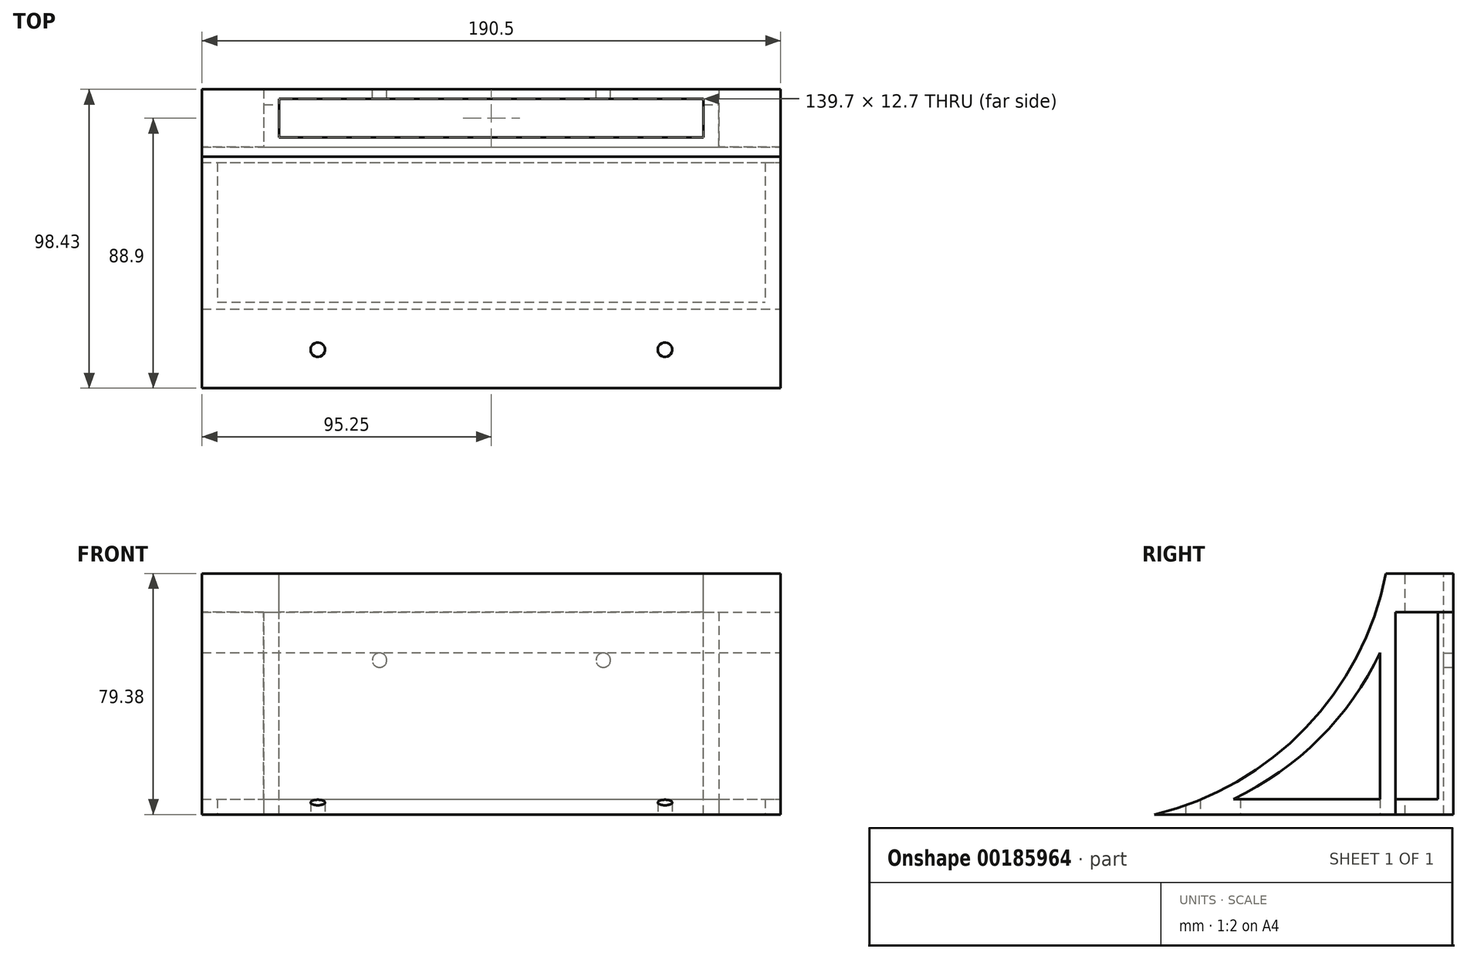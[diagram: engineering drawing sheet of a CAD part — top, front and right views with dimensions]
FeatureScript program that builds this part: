
annotation { "Feature Type Name" : "Feature", "Feature Type Description" : "" }
export const myFeature = defineFeature(function(context is Context, id is Id, definition is map)
    precondition{}
    {
        {
            var Q0;
            Q0=qCreatedBy(makeId("Right.planeOp"),FACE);
            var sketch = newSketch(context, id + "F0", { "sketchPlane" : qUnion([Q0])});
            skLineSegment(sketch, "E0", {"start": v(0, 0) * mm, "end": v(-76.2, 0) * mm});
            skLineSegment(sketch, "E1", {"start": v(0, 0) * mm, "end": v(0, 79.38) * mm});
            skArc(sketch, "E2", {"start": v(-76.2, 0) * mm, "mid": v(-26.42, 28.48) * mm, "end": v(0, 79.38) * mm});
            skSolve(sketch);
        }
        {
            var Q0;
            Q0 = qSketchRegion(id + "F0", true);
            extrude(context, id + "F1", {"entities" : qUnion([Q0]), "depth" : 190.5 * mm});
        }
        {
            var Q0;
            Q0=makeQuery(id+"F1.opExtrude","SWEPT_FACE",FACE,{"disambiguationData":[OSD([sQuery(id+"F0.wireOp",EDGE,"E1")])]});
            var sketch = newSketch(context, id + "F2", { "sketchPlane" : qUnion([Q0])});
            skSolve(sketch);
        }
        {
            var Q0;
            Q0 = qSketchRegion(id + "F2", true);
            var Q1;
            {var subQ0=sQuery(id+"F0.wireOp",EDGE,"E1");Q1=makeQuery(id+"F2.imprint","IMPRINT",FACE,{"disambiguationData":[TD([[makeQuery(id+"F2.imprint","IMPRINT",EDGE,{"derivedFrom":makeQuery(id+"F1.opExtrude","CAP_EDGE",EDGE,{"disambiguationData":[OSD([subQ0])],"isStart":true})}),1.0]])]});}
            extrude(context, id + "F3", {"entities" : qUnion([Q0, Q1]), "operationType" : NewBodyOperationType.ADD, "depth" : 3.17 * mm});
        }
        {
            var Q0;
            Q0=makeQuery(id+"F3.opExtrude","CAP_FACE",FACE,{"disambiguationData":[OSD([sQuery(id+"F0.wireOp",EDGE,"E0"),sQuery(id+"F0.wireOp",EDGE,"E1"),sQuery(id+"F0.wireOp",EDGE,"E2")])],"isStart":false});
            var sketch = newSketch(context, id + "F4", { "sketchPlane" : qUnion([Q0])});
            skLineSegment(sketch, "E3.bottom", {"start": v(-170.18, 79.38) * mm, "end": v(-20.32, 79.38) * mm});
            skLineSegment(sketch, "E3.top", {"start": v(-170.18, 0) * mm, "end": v(-20.32, 0) * mm});
            skLineSegment(sketch, "E3.left", {"start": v(-170.18, 79.38) * mm, "end": v(-170.18, 0) * mm});
            skLineSegment(sketch, "E3.right", {"start": v(-20.32, 79.38) * mm, "end": v(-20.32, 0) * mm});
            skSolve(sketch);
        }
        {
            var Q0;
            Q0=makeQuery(id+"F4.imprint","IMPRINT",FACE,{"disambiguationData":[TD([[makeQuery(id+"F4.imprint","IMPRINT",EDGE,{"derivedFrom":sQuery(id+"F4.wireOp",EDGE,"E3.bottom")}),-1.0]])]});
            extrude(context, id + "F5", {"entities" : qUnion([Q0]), "operationType" : NewBodyOperationType.ADD, "depth" : 19.05 * mm});
        }
        {
            var Q0;
            Q0=makeQuery(id+"F5.boolean.opBoolean","MERGE",FACE,{"derivedFrom":[makeQuery(id+"F3.opExtrude","SWEPT_FACE",FACE,{"disambiguationData":[OSD([sQuery(id+"F0.wireOp",EDGE,"E1"),sQuery(id+"F0.wireOp",EDGE,"E2")])]}),makeQuery(id+"F5.opExtrude","SWEPT_FACE",FACE,{"disambiguationData":[OSD([sQuery(id+"F4.wireOp",EDGE,"E3.bottom")])]})]});
            var sketch = newSketch(context, id + "F6", { "sketchPlane" : qUnion([Q0])});
            skLineSegment(sketch, "E4.bottom", {"start": v(25.4, 19.05) * mm, "end": v(165.1, 19.05) * mm});
            skLineSegment(sketch, "E4.top", {"start": v(25.4, 6.35) * mm, "end": v(165.1, 6.35) * mm});
            skLineSegment(sketch, "E4.left", {"start": v(25.4, 19.05) * mm, "end": v(25.4, 6.35) * mm});
            skLineSegment(sketch, "E4.right", {"start": v(165.1, 19.05) * mm, "end": v(165.1, 6.35) * mm});
            skSolve(sketch);
        }
        {
            var Q0;
            Q0 = qSketchRegion(id + "F6", true);
            extrude(context, id + "F7", {"entities" : qUnion([Q0]), "operationType" : NewBodyOperationType.REMOVE, "oppositeDirection" : true, "depth" : 127 * mm});
        }
        {
            var Q0;
            Q0=makeQuery(id+"F5.opExtrude","CAP_FACE",FACE,{"disambiguationData":[OSD([sQuery(id+"F4.wireOp",EDGE,"E3.bottom"),sQuery(id+"F4.wireOp",EDGE,"E3.top"),sQuery(id+"F4.wireOp",EDGE,"E3.left"),sQuery(id+"F4.wireOp",EDGE,"E3.right")])],"isStart":false});
            var sketch = newSketch(context, id + "F8", { "sketchPlane" : qUnion([Q0])});
            skPoint(sketch, "E5", {"position": v(-132.08, 50.8) * mm});
            skPoint(sketch, "E6", {"position": v(-58.42, 50.8) * mm});
            skLineSegment(sketch, "E7", {"start": v(-132.08, 50.8) * mm, "end": v(-58.42, 50.8) * mm});
            skCircle(sketch, "E8", {"center": v(-132.08, 50.8) * mm, "radius": 2.38 * mm});
            skCircle(sketch, "E9", {"center": v(-58.42, 50.8) * mm, "radius": 2.38 * mm});
            skSolve(sketch);
        }
        {
            var Q0;
            Q0=makeQuery(id+"F8.imprint","IMPRINT",FACE,{"disambiguationData":[TD([[makeQuery(id+"F8.imprint","IMPRINT",EDGE,{"derivedFrom":sQuery(id+"F8.wireOp",EDGE,"E8")}),1.0]])]});
            var Q1;
            Q1=makeQuery(id+"F8.imprint","IMPRINT",FACE,{"disambiguationData":[TD([[makeQuery(id+"F8.imprint","IMPRINT",EDGE,{"derivedFrom":sQuery(id+"F8.wireOp",EDGE,"E9")}),1.0]])]});
            extrude(context, id + "F9", {"entities" : qUnion([Q0, Q1]), "operationType" : NewBodyOperationType.REMOVE, "oppositeDirection" : true, "depth" : 12.7 * mm});
        }
        {
            var Q0;
            {var subQ0=sQuery(id+"F0.wireOp",EDGE,"E0");Q0=makeQuery(id+"F5.boolean.opBoolean","MERGE",FACE,{"derivedFrom":[makeQuery(id+"F3.boolean.opBoolean","MERGE",FACE,{"derivedFrom":[makeQuery(id+"F1.opExtrude","SWEPT_FACE",FACE,{"disambiguationData":[OSD([subQ0])]}),makeQuery(id+"F3.opExtrude","SWEPT_FACE",FACE,{"disambiguationData":[OSD([subQ0,sQuery(id+"F0.wireOp",EDGE,"E1")])]})]}),makeQuery(id+"F5.opExtrude","SWEPT_FACE",FACE,{"disambiguationData":[OSD([sQuery(id+"F4.wireOp",EDGE,"E3.top")])]})]});}
            var sketch = newSketch(context, id + "F10", { "sketchPlane" : qUnion([Q0])});
            skPoint(sketch, "E10", {"position": v(38.1, 63.5) * mm});
            skPoint(sketch, "E11", {"position": v(152.4, 63.5) * mm});
            skLineSegment(sketch, "E12", {"start": v(38.1, 63.5) * mm, "end": v(152.4, 63.5) * mm});
            skCircle(sketch, "E13", {"center": v(38.1, 63.5) * mm, "radius": 2.38 * mm});
            skCircle(sketch, "E14", {"center": v(152.4, 63.5) * mm, "radius": 2.38 * mm});
            skSolve(sketch);
        }
        {
            var Q0;
            Q0 = qSketchRegion(id + "F10", true);
            extrude(context, id + "F11", {"entities" : qUnion([Q0]), "operationType" : NewBodyOperationType.REMOVE, "oppositeDirection" : true, "depth" : 25.4 * mm});
        }
        {
            var Q0;
            {var subQ0=sQuery(id+"F0.wireOp",EDGE,"E2");var subQ1=sQuery(id+"F0.wireOp",EDGE,"E1");var subQ2=sQuery(id+"F0.wireOp",EDGE,"E0");Q0=makeQuery(id+"F5.boolean.opBoolean","SPLIT",FACE,{"disambiguationData":[TD([makeQuery(id+"F5.opExtrude","SWEPT_FACE",FACE,{"disambiguationData":[OSD([sQuery(id+"F4.wireOp",EDGE,"E3.left")])]})])],"derivedFrom":makeQuery(id+"F3.opExtrude","CAP_FACE",FACE,{"disambiguationData":[OSD([subQ2,subQ1,subQ0])],"isStart":false})});}
            var sketch = newSketch(context, id + "F12", { "sketchPlane" : qUnion([Q0])});
            skLineSegment(sketch, "E15.bottom", {"start": v(-170.18, 79.38) * mm, "end": v(-190.5, 79.38) * mm});
            skLineSegment(sketch, "E15.top", {"start": v(-170.18, 66.67) * mm, "end": v(-190.5, 66.67) * mm});
            skLineSegment(sketch, "E15.left", {"start": v(-170.18, 79.38) * mm, "end": v(-170.18, 66.67) * mm});
            skLineSegment(sketch, "E15.right", {"start": v(-190.5, 79.38) * mm, "end": v(-190.5, 66.67) * mm});
            skSolve(sketch);
        }
        {
            var Q0;
            Q0 = qSketchRegion(id + "F12", true);
            extrude(context, id + "F13", {"entities" : qUnion([Q0]), "operationType" : NewBodyOperationType.ADD, "depth" : 19.05 * mm});
        }
        {
            var Q0;
            {var subQ0=sQuery(id+"F0.wireOp",EDGE,"E2");var subQ1=sQuery(id+"F0.wireOp",EDGE,"E1");var subQ2=sQuery(id+"F0.wireOp",EDGE,"E0");Q0=makeQuery(id+"F5.boolean.opBoolean","SPLIT",FACE,{"disambiguationData":[TD([makeQuery(id+"F5.opExtrude","SWEPT_FACE",FACE,{"disambiguationData":[OSD([sQuery(id+"F4.wireOp",EDGE,"E3.right")])]})])],"derivedFrom":makeQuery(id+"F3.opExtrude","CAP_FACE",FACE,{"disambiguationData":[OSD([subQ2,subQ1,subQ0])],"isStart":false})});}
            var sketch = newSketch(context, id + "F14", { "sketchPlane" : qUnion([Q0])});
            skLineSegment(sketch, "E16.bottom", {"start": v(-20.32, 79.38) * mm, "end": v(0, 79.38) * mm});
            skLineSegment(sketch, "E16.top", {"start": v(-20.32, 66.67) * mm, "end": v(0, 66.67) * mm});
            skLineSegment(sketch, "E16.left", {"start": v(-20.32, 79.38) * mm, "end": v(-20.32, 66.67) * mm});
            skLineSegment(sketch, "E16.right", {"start": v(0, 79.38) * mm, "end": v(0, 66.67) * mm});
            skSolve(sketch);
        }
        {
            var Q0;
            Q0 = qSketchRegion(id + "F14", true);
            extrude(context, id + "F15", {"entities" : qUnion([Q0]), "operationType" : NewBodyOperationType.ADD, "depth" : 19.05 * mm});
        }
        {
            var Q0;
            {var subQ0=sQuery(id+"F0.wireOp",EDGE,"E1");Q0=makeQuery(id+"F13.boolean.opBoolean","MERGE",FACE,{"derivedFrom":[makeQuery(id+"F3.boolean.opBoolean","MERGE",FACE,{"derivedFrom":[makeQuery(id+"F1.opExtrude","CAP_FACE",FACE,{"disambiguationData":[OSD([sQuery(id+"F0.wireOp",EDGE,"E0"),subQ0,sQuery(id+"F0.wireOp",EDGE,"E2")])],"isStart":false}),makeQuery(id+"F3.opExtrude","SWEPT_FACE",FACE,{"disambiguationData":[OSD([subQ0]),TDD([makeQuery(id+"F2.imprint","IMPRINT",EDGE,{"derivedFrom":makeQuery(id+"F1.opExtrude","CAP_EDGE",EDGE,{"disambiguationData":[OSD([subQ0])],"isStart":false})})])]})]}),makeQuery(id+"F13.opExtrude","SWEPT_FACE",FACE,{"disambiguationData":[OSD([sQuery(id+"F12.wireOp",EDGE,"E15.right")])]})]});}
            var sketch = newSketch(context, id + "F16", { "sketchPlane" : qUnion([Q0])});
            skLineSegment(sketch, "E17", {"start": v(-50.17, 5.08) * mm, "end": v(-1.9, 5.08) * mm});
            skLineSegment(sketch, "E18", {"start": v(-1.9, 5.08) * mm, "end": v(-1.9, 53.34) * mm});
            skArc(sketch, "E19", {"start": v(-50.16, 5.08) * mm, "mid": v(-21.86, 25.04) * mm, "end": v(-1.9, 53.34) * mm});
            skSolve(sketch);
        }
        {
            var Q0;
            Q0 = qSketchRegion(id + "F16", true);
            extrude(context, id + "F17", {"entities" : qUnion([Q0]), "operationType" : NewBodyOperationType.REMOVE, "oppositeDirection" : true, "depth" : 203.2 * mm});
        }
        {
            var Q0;
            Q0=makeQuery(id+"F5.opExtrude","SWEPT_FACE",FACE,{"disambiguationData":[OSD([sQuery(id+"F4.wireOp",EDGE,"E3.left")])]});
            var sketch = newSketch(context, id + "F18", { "sketchPlane" : qUnion([Q0])});
            skLineSegment(sketch, "E20.bottom", {"start": v(3.18, 66.68) * mm, "end": v(17.15, 66.68) * mm});
            skLineSegment(sketch, "E20.top", {"start": v(3.18, 5.08) * mm, "end": v(17.15, 5.08) * mm});
            skLineSegment(sketch, "E20.left", {"start": v(3.18, 66.68) * mm, "end": v(3.18, 5.08) * mm});
            skLineSegment(sketch, "E20.right", {"start": v(17.15, 66.68) * mm, "end": v(17.15, 5.08) * mm});
            skSolve(sketch);
        }
        {
            var Q0;
            Q0 = qSketchRegion(id + "F18", true);
            extrude(context, id + "F19", {"entities" : qUnion([Q0]), "operationType" : NewBodyOperationType.REMOVE, "oppositeDirection" : true, "depth" : 254 * mm});
        }
        {
            var Q0;
            {var subQ0=sQuery(id+"F0.wireOp",EDGE,"E0");Q0=makeQuery(id+"F5.boolean.opBoolean","MERGE",FACE,{"derivedFrom":[makeQuery(id+"F3.boolean.opBoolean","MERGE",FACE,{"derivedFrom":[makeQuery(id+"F1.opExtrude","SWEPT_FACE",FACE,{"disambiguationData":[OSD([subQ0])]}),makeQuery(id+"F3.opExtrude","SWEPT_FACE",FACE,{"disambiguationData":[OSD([subQ0,sQuery(id+"F0.wireOp",EDGE,"E1")])]})]}),makeQuery(id+"F5.opExtrude","SWEPT_FACE",FACE,{"disambiguationData":[OSD([sQuery(id+"F4.wireOp",EDGE,"E3.top")])]})]});}
            var sketch = newSketch(context, id + "F20", { "sketchPlane" : qUnion([Q0])});
            skLineSegment(sketch, "E21.bottom", {"start": v(5.08, 1.9) * mm, "end": v(185.42, 1.9) * mm});
            skLineSegment(sketch, "E21.top", {"start": v(5.08, 47.9) * mm, "end": v(185.42, 47.9) * mm});
            skLineSegment(sketch, "E21.left", {"start": v(5.08, 1.9) * mm, "end": v(5.08, 47.9) * mm});
            skLineSegment(sketch, "E21.right", {"start": v(185.42, 1.9) * mm, "end": v(185.42, 47.9) * mm});
            skSolve(sketch);
        }
        {
            var Q0;
            Q0 = qSketchRegion(id + "F20", true);
            extrude(context, id + "F21", {"entities" : qUnion([Q0]), "operationType" : NewBodyOperationType.REMOVE, "oppositeDirection" : true, "depth" : 5.08 * mm});
        }
    });
